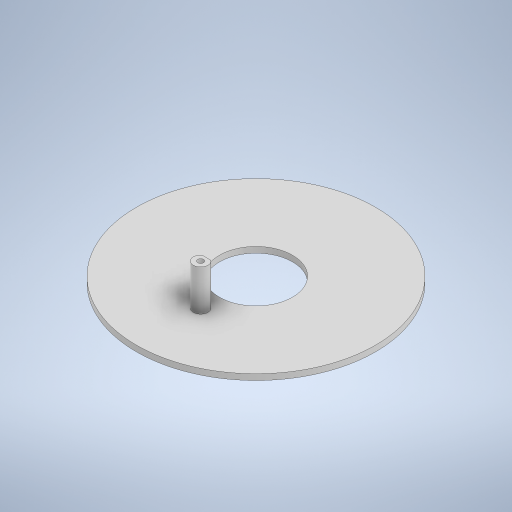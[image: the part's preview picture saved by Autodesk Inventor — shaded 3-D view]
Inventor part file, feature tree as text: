
AUTODESK INVENTOR PART (.ipt)
format: ipt  version: 2024 (Build 280153000, 153)  size: 249,856 bytes
history: native  units: in
note: dims shown in document units (in); Inventor stores cm internally (conversion verified against a paired STEP export)
features: extrude x4, sketch x4
ambient origin geometry x8: Origin, YZ Plane, XZ Plane, XY Plane, X Axis, Y Axis, Z Axis, Center Point
bodies: Solid1 (feature_tree)
feature tree (8):
  extrude  "Extrusion1"  Depth=0.9843in
  extrude  "Extrusion2"  Depth=0.0787in
  extrude  "Extrusion3"  Depth=0.1969in
  extrude  "Extrusion4"  Depth=0.0787in
  sketch  "Sketch1"  dims[d0=3.2283in d1=0.9843in]
  sketch  "Sketch2"  dims[d2=0.0787in d3=0.0in d4=0.748in]
  sketch  "Sketch3"  dims[d5=90.0deg d6=0.1969in]
  sketch  "Sketch4"  dims[d7=0.5512in d8=0.0in d9=0.0787in d10=0.5512in d11=0.0in d12=0.0197in d13=0.1181in d14=0.0197in d15=0.1181in d16=0.5512in d17=0.0in d18=0.0197in d19=0.0344in]
